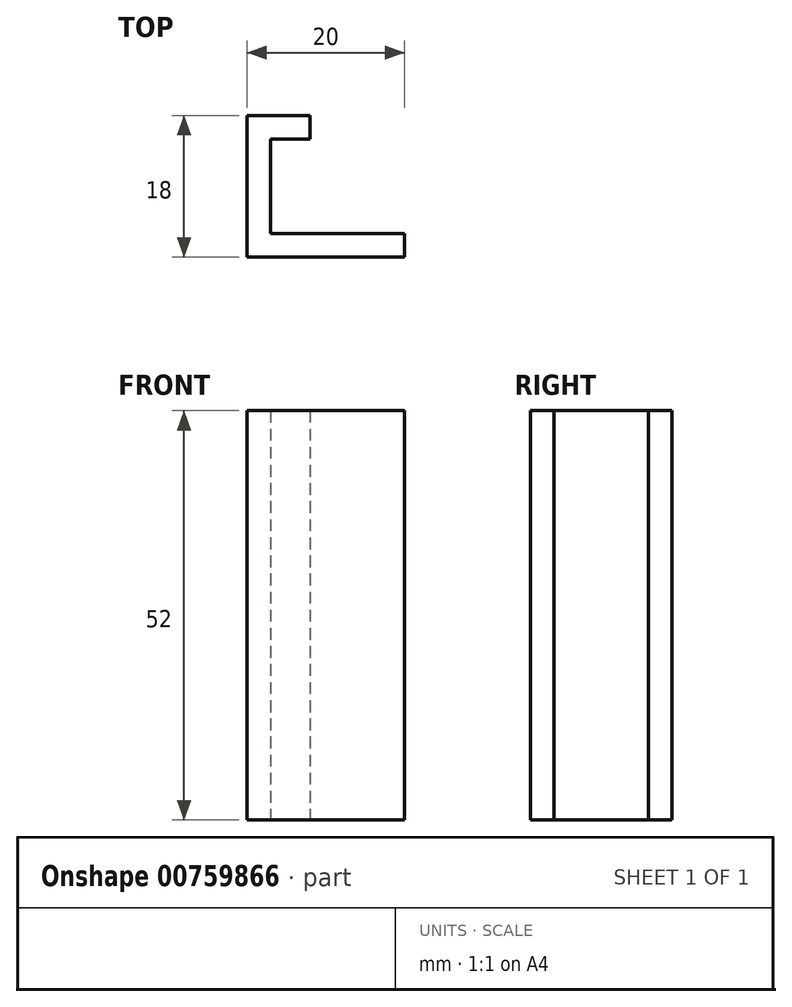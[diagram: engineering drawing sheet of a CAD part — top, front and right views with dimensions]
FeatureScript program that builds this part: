
annotation { "Feature Type Name" : "Feature", "Feature Type Description" : "" }
export const myFeature = defineFeature(function(context is Context, id is Id, definition is map)
    precondition{}
    {
        {
            var Q0;
            Q0=qCreatedBy(makeId("Top.planeOp"),FACE);
            var sketch = newSketch(context, id + "F0", { "sketchPlane" : qUnion([Q0])});
            skLineSegment(sketch, "E0", {"start": v(0, 0) * mm, "end": v(0, 18) * mm});
            skLineSegment(sketch, "E1", {"start": v(0, 18) * mm, "end": v(8, 18) * mm});
            skLineSegment(sketch, "E2", {"start": v(8, 18) * mm, "end": v(8, 15) * mm});
            skLineSegment(sketch, "E3", {"start": v(8, 15) * mm, "end": v(3, 15) * mm});
            skLineSegment(sketch, "E4", {"start": v(3, 15) * mm, "end": v(3, 3) * mm});
            skLineSegment(sketch, "E5", {"start": v(3, 3) * mm, "end": v(20, 3) * mm});
            skLineSegment(sketch, "E6", {"start": v(20, 3) * mm, "end": v(20, 0) * mm});
            skLineSegment(sketch, "E7", {"start": v(20, 0) * mm, "end": v(0, 0) * mm});
            skSolve(sketch);
        }
        {
            var Q0;
            Q0=makeQuery(id+"F0.imprint","IMPRINT",FACE,{"disambiguationData":[TD([[makeQuery(id+"F0.imprint","IMPRINT",EDGE,{"derivedFrom":sQuery(id+"F0.wireOp",EDGE,"E0")}),-1.0]])]});
            extrude(context, id + "F1", {"entities" : qUnion([Q0]), "endBound" : BoundingType.SYMMETRIC, "depth" : 52 * mm, "offsetDistance" : 25 * mm});
        }
    });
